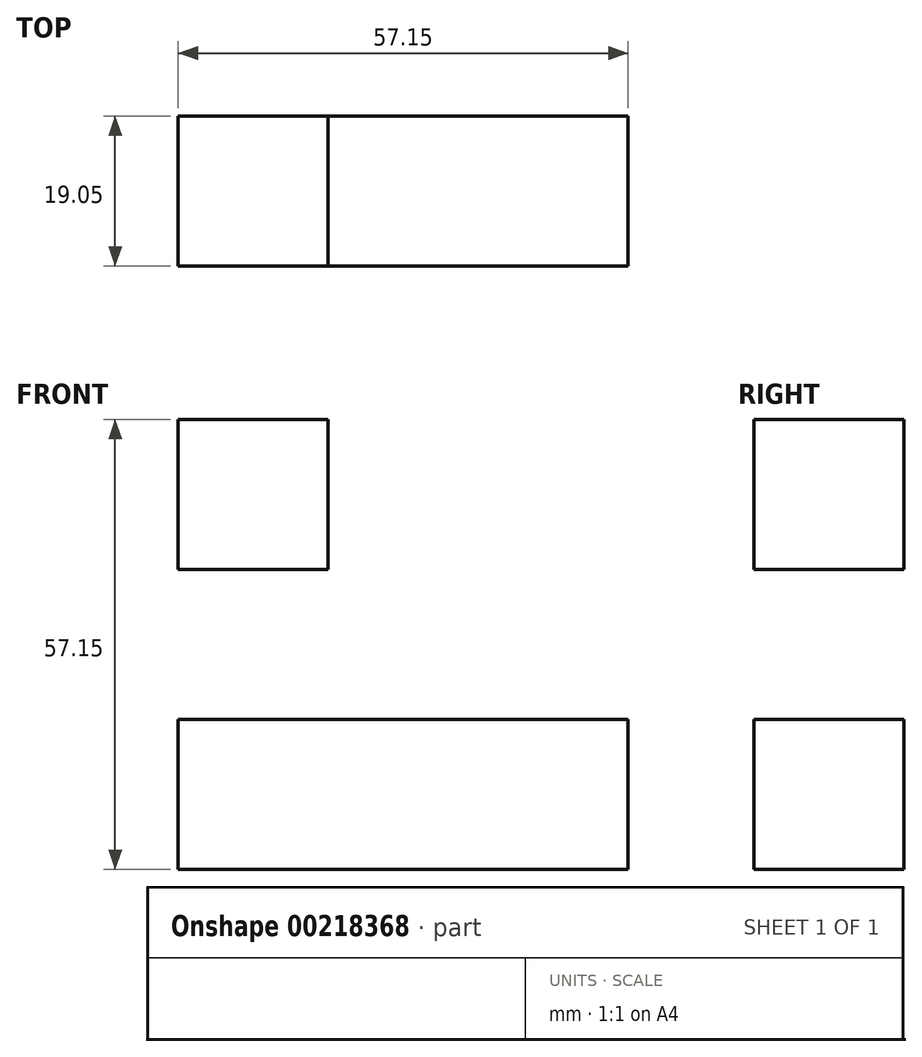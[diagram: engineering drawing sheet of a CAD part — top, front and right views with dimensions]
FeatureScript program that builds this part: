
annotation { "Feature Type Name" : "Feature", "Feature Type Description" : "" }
export const myFeature = defineFeature(function(context is Context, id is Id, definition is map)
    precondition{}
    {
        {
            var Q0;
            Q0=qCreatedBy(makeId("Front.planeOp"),FACE);
            var sketch = newSketch(context, id + "F0", { "sketchPlane" : qUnion([Q0])});
            skLineSegment(sketch, "E0.bottom", {"start": v(-50.98, 72.24) * mm, "end": v(-31.93, 72.24) * mm});
            skLineSegment(sketch, "E0.top", {"start": v(-50.98, 53.19) * mm, "end": v(-31.93, 53.19) * mm});
            skLineSegment(sketch, "E0.left", {"start": v(-50.98, 72.24) * mm, "end": v(-50.98, 53.19) * mm});
            skLineSegment(sketch, "E0.right", {"start": v(-31.93, 72.24) * mm, "end": v(-31.93, 53.19) * mm});
            skLineSegment(sketch, "E1.top", {"start": v(-50.98, 34.14) * mm, "end": v(-31.93, 34.14) * mm});
            skLineSegment(sketch, "E1.left", {"start": v(-50.98, 53.19) * mm, "end": v(-50.98, 34.14) * mm});
            skLineSegment(sketch, "E1.right", {"start": v(-31.93, 53.19) * mm, "end": v(-31.93, 34.14) * mm});
            skLineSegment(sketch, "E2.top", {"start": v(-50.98, 15.09) * mm, "end": v(-31.93, 15.09) * mm});
            skLineSegment(sketch, "E2.left", {"start": v(-50.98, 34.14) * mm, "end": v(-50.98, 15.09) * mm});
            skLineSegment(sketch, "E2.right", {"start": v(-31.93, 34.14) * mm, "end": v(-31.93, 15.09) * mm});
            skLineSegment(sketch, "E3.bottom", {"start": v(-31.93, 34.14) * mm, "end": v(-12.88, 34.14) * mm});
            skLineSegment(sketch, "E3.top", {"start": v(-31.93, 15.09) * mm, "end": v(-12.88, 15.09) * mm});
            skLineSegment(sketch, "E3.right", {"start": v(-12.88, 34.14) * mm, "end": v(-12.88, 15.09) * mm});
            skLineSegment(sketch, "E4.bottom", {"start": v(-12.88, 34.14) * mm, "end": v(6.17, 34.14) * mm});
            skLineSegment(sketch, "E4.top", {"start": v(-12.88, 15.09) * mm, "end": v(6.17, 15.09) * mm});
            skLineSegment(sketch, "E4.right", {"start": v(6.17, 34.14) * mm, "end": v(6.17, 15.09) * mm});
            skSolve(sketch);
        }
        {
            var Q0;
            Q0=makeQuery(id+"F0.imprint","IMPRINT",FACE,{"disambiguationData":[TD([[makeQuery(id+"F0.imprint","IMPRINT",EDGE,{"derivedFrom":sQuery(id+"F0.wireOp",EDGE,"E0.bottom")}),-1.0]])]});
            var Q1;
            Q1=makeQuery(id+"F0.imprint","IMPRINT",FACE,{"disambiguationData":[TD([[makeQuery(id+"F0.imprint","IMPRINT",EDGE,{"derivedFrom":sQuery(id+"F0.wireOp",EDGE,"E0.top")}),-1.0]])]});
            var Q2;
            Q2=makeQuery(id+"F0.imprint","IMPRINT",FACE,{"disambiguationData":[TD([[makeQuery(id+"F0.imprint","IMPRINT",EDGE,{"derivedFrom":sQuery(id+"F0.wireOp",EDGE,"E1.top")}),-1.0]])]});
            var Q3;
            Q3=makeQuery(id+"F0.imprint","IMPRINT",FACE,{"disambiguationData":[TD([[makeQuery(id+"F0.imprint","IMPRINT",EDGE,{"derivedFrom":sQuery(id+"F0.wireOp",EDGE,"E3.bottom")}),-1.0]])]});
            var Q4;
            Q4=makeQuery(id+"F0.imprint","IMPRINT",FACE,{"disambiguationData":[TD([[makeQuery(id+"F0.imprint","IMPRINT",EDGE,{"derivedFrom":sQuery(id+"F0.wireOp",EDGE,"E4.bottom")}),-1.0]])]});
            extrude(context, id + "F1", {"entities" : qUnion([Q0, Q1, Q2, Q3, Q4]), "depth" : 19.05 * mm});
        }
    });
